# Revit family: Haworth_Lana_Floor_Light
name_source: partatom
category: Lighting Fixtures
revit_build: Autodesk Revit 2018 (Build: 20170223_1515(x64)
units: mm (PartAtom-declared; Revit-internal decimal feet)

## family parameters
Always vertical = Yes
Cut with Voids When Loaded = No
Light Source = Yes
OmniClass Number = 23.80.70.11.14
OmniClass Title = General Luminaries, Directional
Part Type = Normal
Room Calculation Point = No
Round Connector Dimension = Use Diameter
Shared = No
Work Plane-Based = No

## types (2) — shared parameters
Assembly Code = D5020200
Base Finish = Haworth _ Metal _ Chrome
Circle Base Radius = 6 1/2"
Circle Top Radius = 3 3/4"
Color Filter = 16777215
Dimming Lamp Color Temperature Shift = Incandescent Lamp Curve
Emit Shape Visible in Rendering = No
Emit from Circle Diameter = 24"
Floor Lamp = Yes
Glass Finish = Haworth _ Glass _ Clear
Light Source Symbol Length = 12"
Manufacturer = Haworth
Pedestal Finish = Haworth _ Metal _ Chrome
Revision Number = 1
Size = Verify Final Dim. w/Haworth
Spot Beam Angle = 60.00°
Spot Field Angle = 60.00°
Stand Height = 55"
Stand Inside Radius = 5 1/4"
Stand Radius = 5 1/2"
Stand Top Height = 54 79/256"
Stand Top Radius = 177/256"
Tilt Angle = 90.00°
URL = http://www.haworth.com
URL - Product = https://www.haworth.com
Warranty = https://www.haworth.com

## per-type parameters (varying)
| type | Description | Pedestal |
| HCPL-LNF0 | Haworth Lana Light - Floor Lamp | No |
| HCPL-LNF1 | Haworth Lana Light - Floor Lamp with Pedestal | Yes |

note: column(s) folded — value = type name in every type: Model

## geometry (parser evidence)
native form markers: Sweep x4
no freeform markers — native parametric forms only
